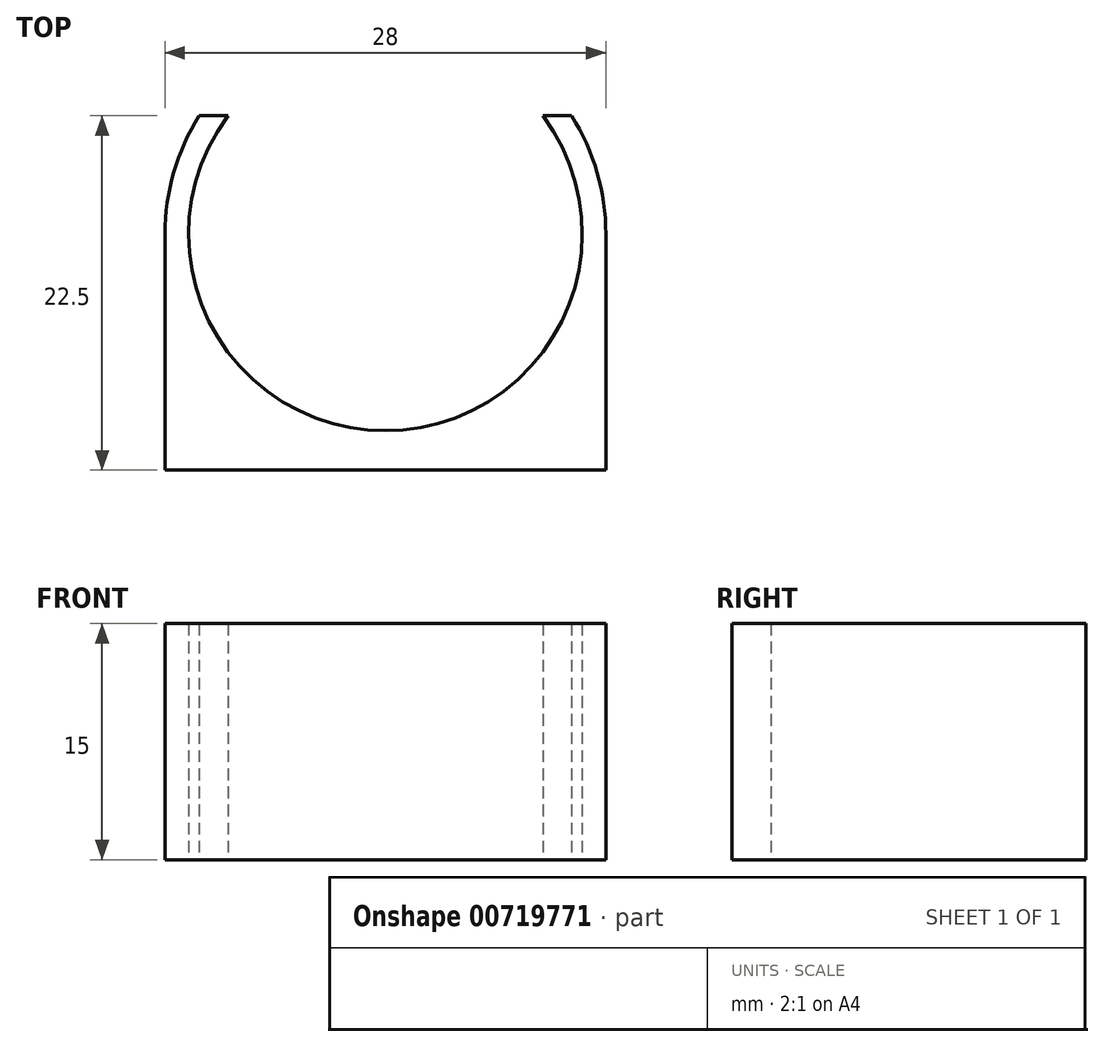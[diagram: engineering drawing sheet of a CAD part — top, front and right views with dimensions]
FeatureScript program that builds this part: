
annotation { "Feature Type Name" : "Feature", "Feature Type Description" : "" }
export const myFeature = defineFeature(function(context is Context, id is Id, definition is map)
    precondition{}
    {
        {
            var Q0;
            Q0=qCreatedBy(makeId("Top.planeOp"),FACE);
            var sketch = newSketch(context, id + "F0", { "sketchPlane" : qUnion([Q0])});
            skArc(sketch, "E0", {"start": v(4, 22.5) * mm, "mid": v(14, 2.5) * mm, "end": v(24, 22.5) * mm});
            skArc(sketch, "E1", {"start": v(2.18, 22.5) * mm, "mid": v(0.56, 18.9) * mm, "end": v(0, 15) * mm});
            skLineSegment(sketch, "E2", {"start": v(0, 15) * mm, "end": v(0, 0) * mm});
            skLineSegment(sketch, "E3", {"start": v(2.18, 22.5) * mm, "end": v(25.82, 22.5) * mm});
            skLineSegment(sketch, "E4", {"start": v(28, 15) * mm, "end": v(28, 0) * mm});
            skLineSegment(sketch, "E5", {"start": v(28, 0) * mm, "end": v(0, 0) * mm});
            skArc(sketch, "E6.trimOffspring", {"start": v(28, 15) * mm, "mid": v(27.44, 18.9) * mm, "end": v(25.82, 22.5) * mm});
            skSolve(sketch);
        }
        {
            var Q0;
            {var subQ1=sQuery(id+"F0.wireOp",EDGE,"E0");Q0=makeQuery(id+"F0.imprint","IMPRINT",FACE,{"disambiguationData":[TD([[makeQuery(id+"F0.imprint","IMPRINT",EDGE,{"derivedFrom":subQ1}),-1.0]])]});}
            extrude(context, id + "F1", {"entities" : qUnion([Q0]), "depth" : 15 * mm, "offsetDistance" : 25 * mm});
        }
    });
